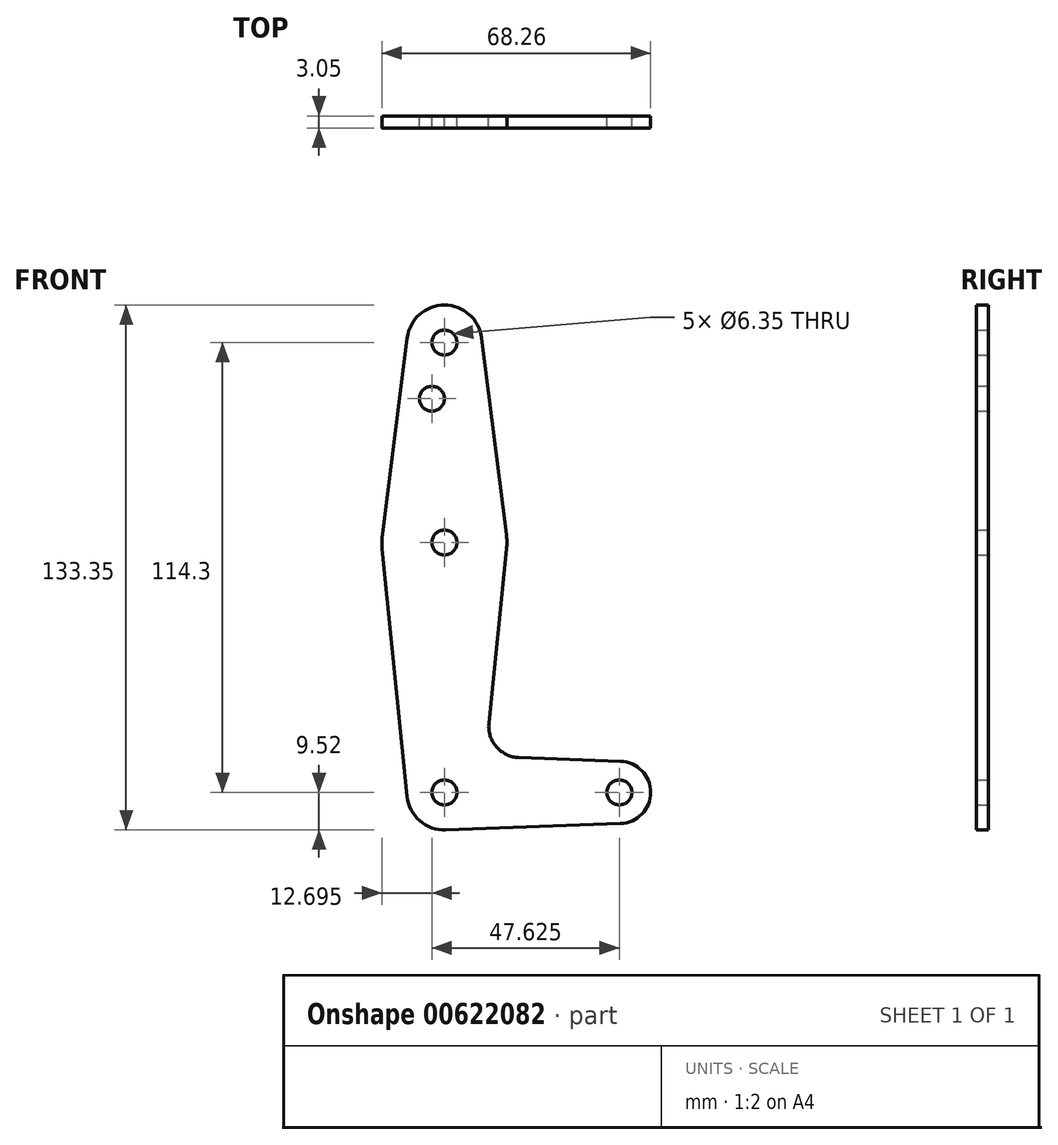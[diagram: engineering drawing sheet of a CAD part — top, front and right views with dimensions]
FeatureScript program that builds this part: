
annotation { "Feature Type Name" : "Feature", "Feature Type Description" : "" }
export const myFeature = defineFeature(function(context is Context, id is Id, definition is map)
    precondition{}
    {
        {
            var Q0;
            Q0=qCreatedBy(makeId("Front.planeOp"),FACE);
            var sketch = newSketch(context, id + "F0", { "sketchPlane" : qUnion([Q0])});
            skCircle(sketch, "E0", {"center": v(0, 0) * mm, "radius": 9.53 * mm});
            skCircle(sketch, "E1", {"center": v(0, 63.5) * mm, "radius": 15.88 * mm});
            skCircle(sketch, "E2", {"center": v(0, 114.3) * mm, "radius": 9.53 * mm});
            skCircle(sketch, "E3", {"center": v(44.45, 0) * mm, "radius": 7.94 * mm});
            skLineSegment(sketch, "E4", {"start": v(-15.75, 65.48) * mm, "end": v(-9.45, 115.5) * mm});
            skLineSegment(sketch, "E5", {"start": v(9.45, 115.5) * mm, "end": v(15.75, 65.48) * mm});
            skLineSegment(sketch, "E6", {"start": v(-15.8, 61.91) * mm, "end": v(-9.48, -0.95) * mm});
            skLineSegment(sketch, "E7", {"start": v(11.3, 17.6) * mm, "end": v(15.8, 61.9) * mm});
            skLineSegment(sketch, "E8", {"start": v(18.93, 8.85) * mm, "end": v(44.73, 7.93) * mm});
            skLineSegment(sketch, "E9", {"start": v(0.34, -9.52) * mm, "end": v(44.73, -7.93) * mm});
            skCircle(sketch, "E10", {"center": v(0, 114.3) * mm, "radius": 3.18 * mm});
            skCircle(sketch, "E11", {"center": v(0, 63.5) * mm, "radius": 3.18 * mm});
            skCircle(sketch, "E12", {"center": v(0, 0) * mm, "radius": 3.18 * mm});
            skCircle(sketch, "E13", {"center": v(44.45, 0) * mm, "radius": 3.18 * mm});
            skCircle(sketch, "E14", {"center": v(-3.17, 100.03) * mm, "radius": 3.18 * mm});
            skPoint(sketch, "E15.newPointA", {"position": v(9.53, 0) * mm});
            skArc(sketch, "E15.filletArc", {"start": v(11.3, 17.6) * mm, "mid": v(13.22, 11.57) * mm, "end": v(18.93, 8.85) * mm});
            skSolve(sketch);
        }
        {
            var Q0;
            Q0 = qSketchRegion(id + "F0", true);
            extrude(context, id + "F1", {"entities" : qUnion([Q0]), "depth" : 3.05 * mm, "offsetDistance" : 25.4 * mm});
        }
    });
